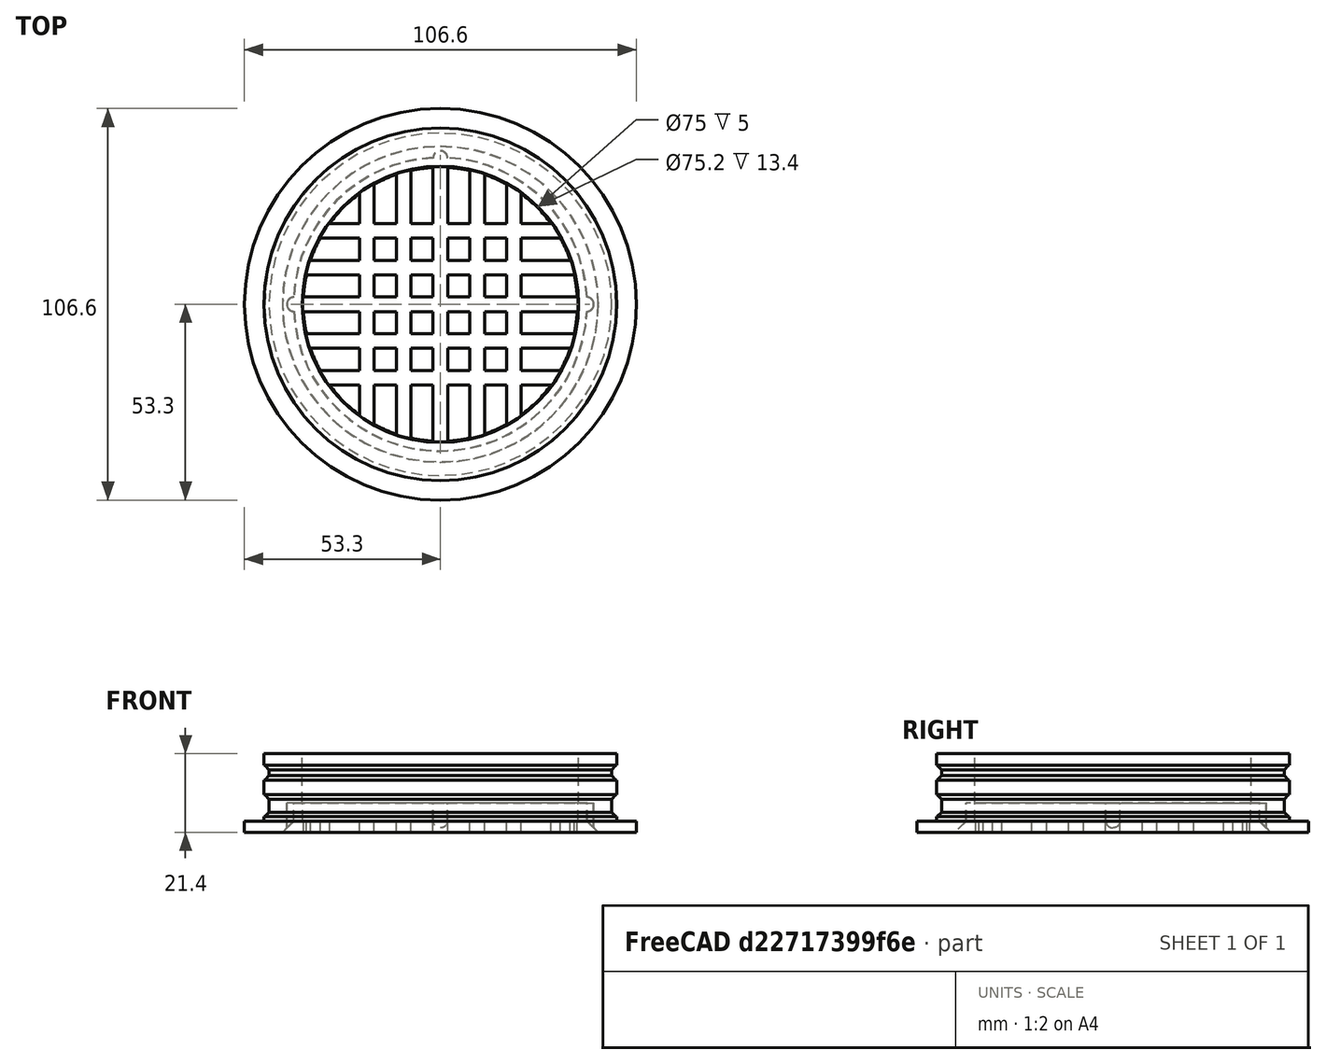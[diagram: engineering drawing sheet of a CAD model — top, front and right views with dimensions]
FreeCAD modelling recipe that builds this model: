
FCSTD DOCUMENT  (FreeCAD 0.18R4 (GitTag))
Label: rejilla
License: CreativeCommons Attribution-ShareAlike
LicenseURL: http://creativecommons.org/licenses/by-sa/4.0/
objects: Part::Cylinder×30, Part::Cut×16, Part::MultiFuse×11, Part::Box×10, Part::Cone×2, Part::Chamfer×2
note: 71 computed .brp shape members not serialized (recipe doc carries the construction recipe); baked Part::Feature solids carry a one-line shape summary decoded from their .brp

FEATURE [Part::Box] Box023  label="Cube023"
  AttacherType = Attacher::AttachEngine3D
  Height = 5
  Length = 74
  Placement = pos=(12,-37,-41) rot=(0,0,1;1.5708rad)
  Width = 4
FEATURE [Part::Cylinder] Cylinder066
  Angle = 360
  AttacherType = Attacher::AttachEngine3D
  Height = 32
  Placement = pos=(0,0,-39) rot=(0,0,1;0rad)
  Radius = 37.5
FEATURE [Part::Cylinder] Cylinder069
  Angle = 360
  AttacherType = Attacher::AttachEngine3D
  Height = 5
  Radius = 39.9
FEATURE [Part::Box] Box028  label="Cube028"
  AttacherType = Attacher::AttachEngine3D
  Height = 5
  Length = 66
  Placement = pos=(22,-33,-41) rot=(0,0,1;1.5708rad)
  Width = 4
FEATURE [Part::Cylinder] Cylinder070
  Angle = 360
  AttacherType = Attacher::AttachEngine3D
  Height = 7.8
  Placement = pos=(39.8,0,-18) rot=(0,0,1;0rad)
  Radius = 1.9
FEATURE [Part::Box] Box020  label="Cube020"
  AttacherType = Attacher::AttachEngine3D
  Height = 5
  Length = 74
  Placement = pos=(-37,8,-41) rot=(0,0,1;0rad)
  Width = 4
FEATURE [Part::Cylinder] Cylinder060
  Angle = 360
  AttacherType = Attacher::AttachEngine3D
  Height = 5
  Placement = pos=(0,0,-41) rot=(0,0,1;0rad)
  Radius = 37.5
FEATURE [Part::Cylinder] Cylinder059
  Angle = 360
  AttacherType = Attacher::AttachEngine3D
  Height = 5
  Placement = pos=(0,0,-41) rot=(0,0,1;0rad)
  Radius = 45
FEATURE [Part::Cylinder] Cylinder061  label="ajustar_radio_de_este006"
  Angle = 360
  AttacherType = Attacher::AttachEngine3D
  Height = 5
  Placement = pos=(0,0,-23.2) rot=(0,0,1;0rad)
  Radius = 68.3
FEATURE [Part::Cylinder] Cylinder062
  Angle = 360
  AttacherType = Attacher::AttachEngine3D
  Height = 7.8
  Placement = pos=(0,39.8,-18) rot=(0,0,1;0rad)
  Radius = 1.9
FEATURE [Part::Box] Box025  label="Cube025"
  AttacherType = Attacher::AttachEngine3D
  Height = 5
  Length = 74
  Placement = pos=(-37,-12,-41) rot=(0,0,1;0rad)
  Width = 4
FEATURE [Part::Cylinder] Cylinder063
  Angle = 360
  AttacherType = Attacher::AttachEngine3D
  Height = 10
  Placement = pos=(0,0,-49) rot=(0,0,1;0rad)
  Radius = 50
FEATURE [Part::Box] Box021  label="Cube021"
  AttacherType = Attacher::AttachEngine3D
  Height = 5
  Length = 66
  Placement = pos=(-33,18,-41) rot=(0,0,1;0rad)
  Width = 4
FEATURE [Part::Box] Box026  label="Cube026"
  AttacherType = Attacher::AttachEngine3D
  Height = 5
  Length = 76
  Placement = pos=(-38,-2,-41) rot=(0,0,1;0rad)
  Width = 4
FEATURE [Part::Cylinder] Cylinder064
  Angle = 360
  AttacherType = Attacher::AttachEngine3D
  Height = 5
  Radius = 37.5
FEATURE [Part::Cut] Cut033
  Base = -> Cylinder069
  Placement = pos=(0,0,-15.2) rot=(0,0,1;0rad)
  Tool = -> Cylinder064
FEATURE [Part::Box] Box022  label="Cube022"
  AttacherType = Attacher::AttachEngine3D
  Height = 5
  Length = 74
  Placement = pos=(-8,-37,-41) rot=(0,0,1;1.5708rad)
  Width = 4
FEATURE [Part::Box] Box024  label="Cube024"
  AttacherType = Attacher::AttachEngine3D
  Height = 5
  Length = 66
  Placement = pos=(-18,-33,-41) rot=(0,0,1;1.5708rad)
  Width = 4
FEATURE [Part::Cylinder] Cylinder065
  Angle = 360
  AttacherType = Attacher::AttachEngine3D
  Height = 5
  Placement = pos=(0,0,-41) rot=(0,0,1;0rad)
  Radius = 37.3
FEATURE [Part::Cut] Cut035  label="anillo002"
  Base = -> Cylinder060
  Tool = -> Cylinder065
FEATURE [Part::Box] Box027  label="Cube027"
  AttacherType = Attacher::AttachEngine3D
  Height = 5
  Length = 66
  Placement = pos=(-33,-22,-41) rot=(0,0,1;0rad)
  Width = 4
FEATURE [Part::Box] Box029  label="Cube029"
  AttacherType = Attacher::AttachEngine3D
  Height = 5
  Length = 76
  Placement = pos=(2,-38,-41) rot=(0,0,1;1.5708rad)
  Width = 4
FEATURE [Part::MultiFuse] Fusion022
  Shapes = -> [Cut035,Box024,Box028,Box022,Box020,Box025,Box027,Box026,Box021,Box029,Box023]
FEATURE [Part::Cylinder] Cylinder067
  Angle = 360
  AttacherType = Attacher::AttachEngine3D
  Height = 5
  Placement = pos=(0,0,-41) rot=(0,0,1;0rad)
  Radius = 37.5
FEATURE [Part::Cut] Cut032
  Base = -> Cylinder059
  Tool = -> Cylinder067
FEATURE [Part::Cut] Cut036
  Base = -> Fusion022
  Tool = -> Cut032
FEATURE [Part::Cut] Cut034
  Base = -> Cut036
  Placement = pos=(0,0,20.8) rot=(0,0,1;0rad)
  Tool = -> Cylinder063
FEATURE [Part::Cylinder] Cylinder068
  Angle = 360
  AttacherType = Attacher::AttachEngine3D
  Height = 7.8
  Placement = pos=(-39.8,0,-18) rot=(0,0,1;0rad)
  Radius = 1.9
FEATURE [Part::Cone] Cone004
  Angle = 360
  AttacherType = Attacher::AttachEngine3D
  Height = 5
  Placement = pos=(0,0,-15.2) rot=(0,1,0;3.14159rad)
  Radius1 = 39.85
  Radius2 = 44.9
FEATURE [Part::Cut] Cut030
  Base = -> Cone004
  Tool = -> Cylinder066
FEATURE [Part::MultiFuse] Fusion020  label="rejilla_interior_sin_cortar_oblicuo_sin_tapa_007"
  Shapes = -> [Cut033,Cut030]
FEATURE [Part::Cut] Cut031
  Base = -> Fusion020
  Tool = -> Cylinder061
FEATURE [Part::MultiFuse] Fusion023  label="rejilla__interior_sin_cortar_oblicuo_sin_muescas002"
  Shapes = -> [Cut034,Cut031]
FEATURE [Part::MultiFuse] Fusion024  label="rejilla__interior_sin_cortar_oblicuo002"
  Shapes = -> [Fusion023,Cylinder068,Cylinder070]
FEATURE [Part::MultiFuse] Fusion021  label="rejilla__interior_v2.0_cono_39.086"
  Shapes = -> [Fusion024,Cylinder062]
FEATURE [Part::Cylinder] Cylinder019  label="ajustar_radio_de_este001"
  Angle = 360
  AttacherType = Attacher::AttachEngine3D
  Height = 5
  Placement = pos=(0,0,-23.2) rot=(0,0,1;0rad)
  Radius = 68.3
FEATURE [Part::Cylinder] Cylinder009
  Angle = 360
  AttacherType = Attacher::AttachEngine3D
  Height = 27.4
  Placement = pos=(0,0,-17) rot=(0,0,1;0rad)
  Radius = 40
FEATURE [Part::Cone] Cone
  Angle = 360
  AttacherType = Attacher::AttachEngine3D
  Height = 5
  Placement = pos=(0,0,-15.2) rot=(0,1,0;3.14159rad)
  Radius1 = 40
  Radius2 = 45
FEATURE [Part::Cylinder] Cylinder055
  Angle = 360
  AttacherType = Attacher::AttachEngine3D
  Height = 13.4
  Placement = pos=(0,0,-10.2) rot=(0,0,1;0rad)
  Radius = 40
FEATURE [Part::Cylinder] Cylinder056
  Angle = 360
  AttacherType = Attacher::AttachEngine3D
  Height = 13.4
  Placement = pos=(0,0,-10.2) rot=(0,0,1;0rad)
  Radius = 37.6
FEATURE [Part::Cylinder] Cylinder054
  Angle = 360
  AttacherType = Attacher::AttachEngine3D
  Height = 7.8
  Placement = pos=(0,39.8,-18) rot=(0,0,1;0rad)
  Radius = 2
FEATURE [Part::Cylinder] Cylinder004
  Angle = 360
  AttacherType = Attacher::AttachEngine3D
  Height = 1.2
  Placement = pos=(0,0,-15.2) rot=(0,0,1;0rad)
  Radius = 48
FEATURE [Part::Cylinder] Cylinder058
  Angle = 360
  AttacherType = Attacher::AttachEngine3D
  Height = 7.8
  Placement = pos=(-39.8,0,-18) rot=(0,0,1;0rad)
  Radius = 2
FEATURE [Part::Cylinder] Cylinder
  Angle = 360
  AttacherType = Attacher::AttachEngine3D
  Height = 3.2
  Radius = 48
FEATURE [Part::Cylinder] Cylinder057
  Angle = 360
  AttacherType = Attacher::AttachEngine3D
  Height = 7.8
  Placement = pos=(39.8,0,-18) rot=(0,0,1;0rad)
  Radius = 2
FEATURE [Part::Cylinder] Cylinder008
  Angle = 360
  AttacherType = Attacher::AttachEngine3D
  Height = 23.4
  Placement = pos=(0,0,-20.2) rot=(0,0,1;0rad)
  Radius = 45
FEATURE [Part::Cylinder] Cylinder002
  Angle = 360
  AttacherType = Attacher::AttachEngine3D
  Height = 4
  Placement = pos=(0,0,-8) rot=(0,0,1;0rad)
  Radius = 48
FEATURE [Part::Cylinder] Cylinder001
  Angle = 360
  AttacherType = Attacher::AttachEngine3D
  Height = 4
  Placement = pos=(0,0,-4) rot=(0,0,1;0rad)
  Radius = 46.6
FEATURE [Part::Cylinder] Cylinder003
  Angle = 360
  AttacherType = Attacher::AttachEngine3D
  Height = 6
  Placement = pos=(0,0,-14) rot=(0,0,1;0rad)
  Radius = 46.6
FEATURE [Part::Cylinder] Cylinder006  label="ajustar_radio_de_este"
  Angle = 360
  AttacherType = Attacher::AttachEngine3D
  Height = 5
  Placement = pos=(0,0,-20.2) rot=(0,0,1;0rad)
  Radius = 51.3
FEATURE [Part::Cylinder] Cylinder005
  Angle = 360
  AttacherType = Attacher::AttachEngine3D
  Height = 25
  Placement = pos=(0,0,-18) rot=(0,0,1;0rad)
  Radius = 45
FEATURE [Part::Cylinder] Cylinder007
  Angle = 360
  AttacherType = Attacher::AttachEngine3D
  Height = 25
  Placement = pos=(0,0,-23) rot=(0,0,1;0rad)
  Radius = 45
FEATURE [Part::Cut] Cut026
  Base = -> Cylinder055
  Tool = -> Cylinder056
FEATURE [Part::Cut] Cut001
  Base = -> Cylinder006
  Tool = -> Cylinder007
FEATURE [Part::MultiFuse] Fusion
  Shapes = -> [Cylinder004,Cylinder,Cylinder003,Cylinder001,Cylinder002]
FEATURE [Part::Cut] Cut
  Base = -> Fusion
  Tool = -> Cylinder005
FEATURE [Part::MultiFuse] Fusion001
  Shapes = -> [Cut001,Cut]
FEATURE [Part::MultiFuse] Fusion002
  Shapes = -> [Cylinder009,Cone]
FEATURE [Part::Cut] Cut002
  Base = -> Cylinder008
  Tool = -> Fusion002
FEATURE [Part::MultiFuse] Fusion003  label="rejilla_sin_cortar_oblicuo_sin_chaflan"
  Shapes = -> [Fusion001,Cut002]
FEATURE [Part::Chamfer] Chamfer
  Base = -> Fusion003
  Edges = 2 edges r=1.2: [Edge12,Edge24]
FEATURE [Part::Chamfer] Chamfer001  label="rejilla__exteriorsin_cortar_oblicuo_alta"
  Base = -> Chamfer
  Edges = 2 edges r=1.2: [Edge8,Edge26]
FEATURE [Part::Cut] Cut009  label="rejilla__exterior_sin_cortar_oblicuo_sin_muescas_01"
  Base = -> Chamfer001
  Tool = -> Cylinder019
FEATURE [Part::MultiFuse] Fusion019  label="rejilla__exterior_sin_cortar_oblicuo_sin_muescas"
  Shapes = -> [Cut009,Cut026]
FEATURE [Part::Cut] Cut027
  Base = -> Fusion019
  Tool = -> Cylinder054
FEATURE [Part::Cut] Cut028
  Base = -> Cut027
  Tool = -> Cylinder057
FEATURE [Part::Cut] Cut029  label="rejilla__exterior_sin_cortar"
  Base = -> Cut028
  Tool = -> Cylinder058
FEATURE [Part::Cylinder] Cylinder071
  Angle = 360
  AttacherType = Attacher::AttachEngine3D
  Height = 3
  Radius = 53.3
FEATURE [Part::Cylinder] Cylinder072
  Angle = 360
  AttacherType = Attacher::AttachEngine3D
  Height = 3
  Radius = 47.3
FEATURE [Part::Cut] Cut037
  Base = -> Cylinder071
  Placement = pos=(0,0,-18.2) rot=(0,0,1;0rad)
  Tool = -> Cylinder072
FEATURE [Part::MultiFuse] Fusion025  label="rejilla__exterior_004"
  Shapes = -> [Cut029,Cut037]
